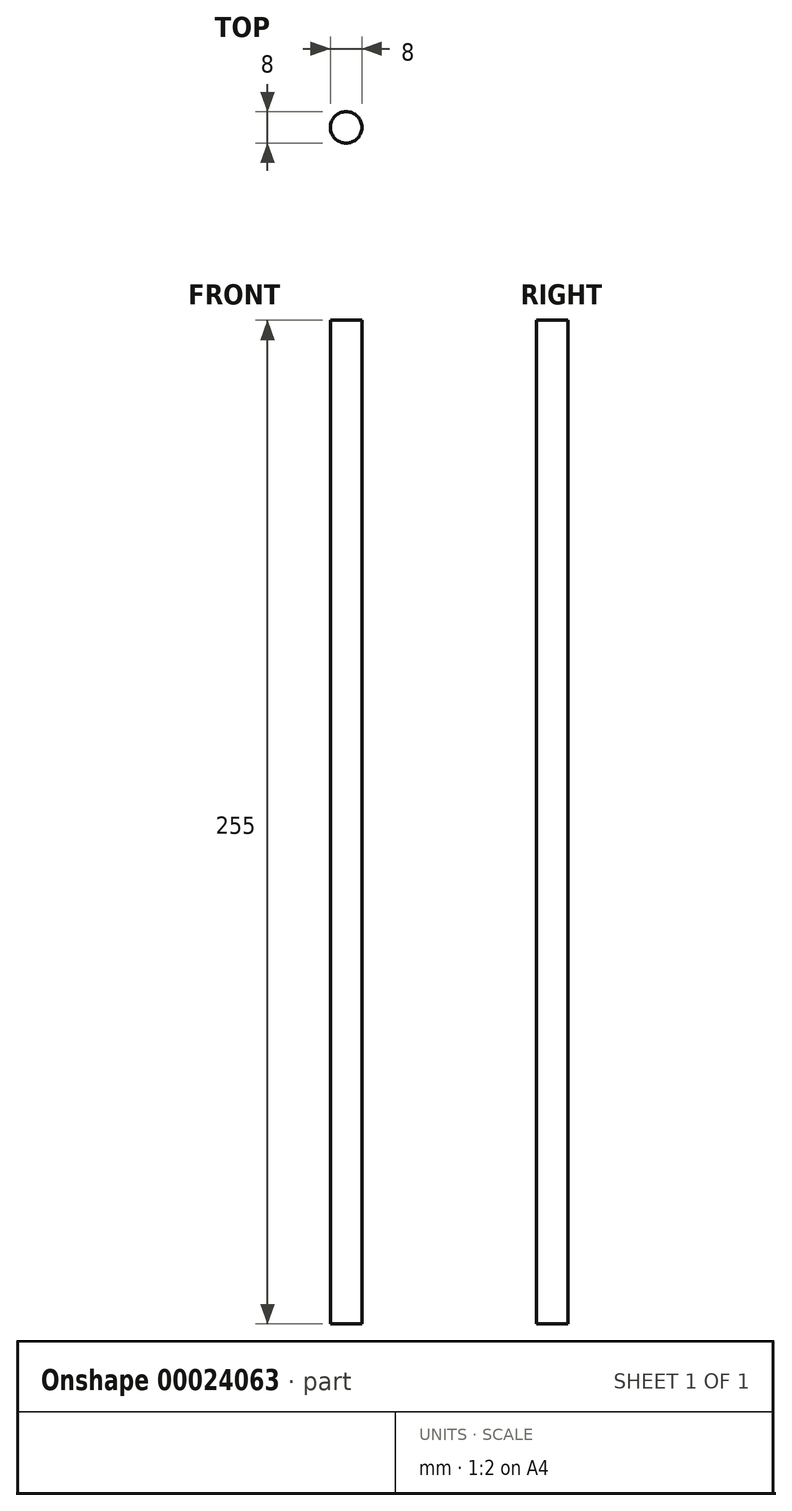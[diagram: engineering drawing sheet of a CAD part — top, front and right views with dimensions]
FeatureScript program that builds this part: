
annotation { "Feature Type Name" : "Feature", "Feature Type Description" : "" }
export const myFeature = defineFeature(function(context is Context, id is Id, definition is map)
    precondition{}
    {
        {
            var Q0;
            Q0=qCreatedBy(makeId("Top.planeOp"),FACE);
            var sketch = newSketch(context, id + "F0", { "sketchPlane" : qUnion([Q0])});
            skCircle(sketch, "E0", {"center": v(0, 0) * mm, "radius": 4 * mm});
            skSolve(sketch);
        }
        {
            var Q0;
            Q0=qSketchRegion(id+"F0",true);
            extrude(context, id + "F1", {"entities" : qUnion([Q0]), "depth" : 255 * mm});
        }
    });
